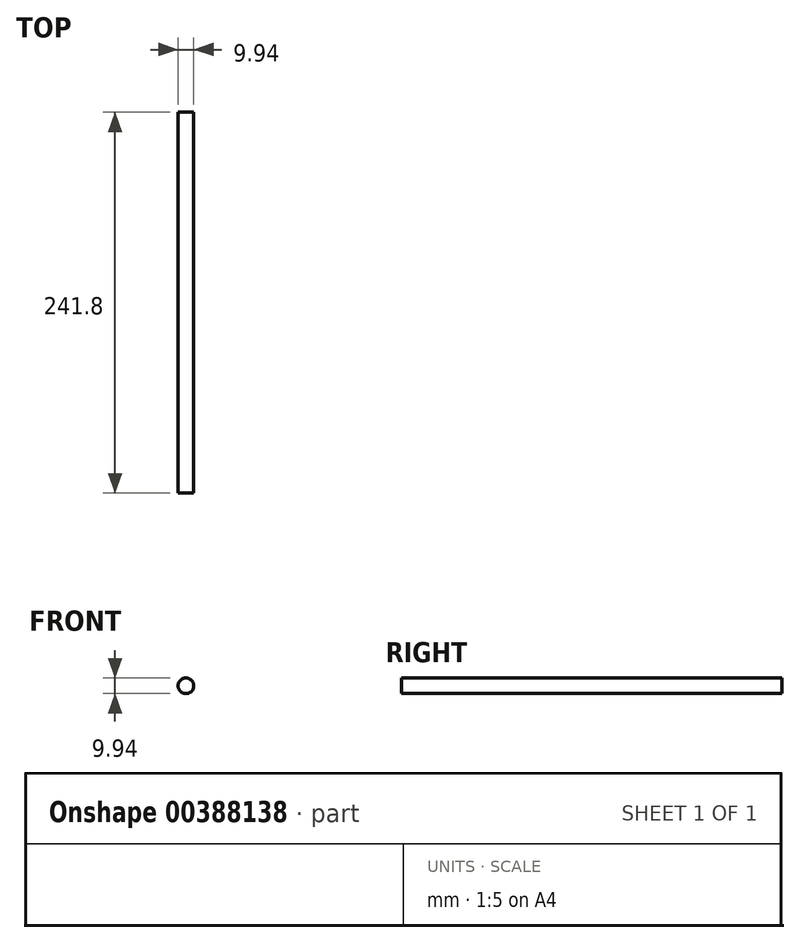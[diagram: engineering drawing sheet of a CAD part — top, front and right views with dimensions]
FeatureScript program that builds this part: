
annotation { "Feature Type Name" : "Feature", "Feature Type Description" : "" }
export const myFeature = defineFeature(function(context is Context, id is Id, definition is map)
    precondition{}
    {
        {
            var Q0;
            Q0=qCreatedBy(makeId("Front.planeOp"),FACE);
            var sketch = newSketch(context, id + "F0", { "sketchPlane" : qUnion([Q0])});
            skCircle(sketch, "E0", {"center": v(0, 0) * mm, "radius": 4.97 * mm});
            skSolve(sketch);
        }
        {
            var Q0;
            Q0=makeQuery(id+"F0.imprint","IMPRINT",FACE,{"disambiguationData":[TD([[makeQuery(id+"F0.imprint","IMPRINT",EDGE,{"derivedFrom":sQuery(id+"F0.wireOp",EDGE,"E0")}),1.0]])]});
            var Q1;
            Q1=sQuery(id+"F0.wireOp",EDGE,"E0");
            extrude(context, id + "F1", {"entities" : qUnion([Q0]), "surfaceEntities" : qUnion([Q1]), "endBound" : BoundingType.SYMMETRIC, "depth" : 241.8 * mm});
        }
    });
